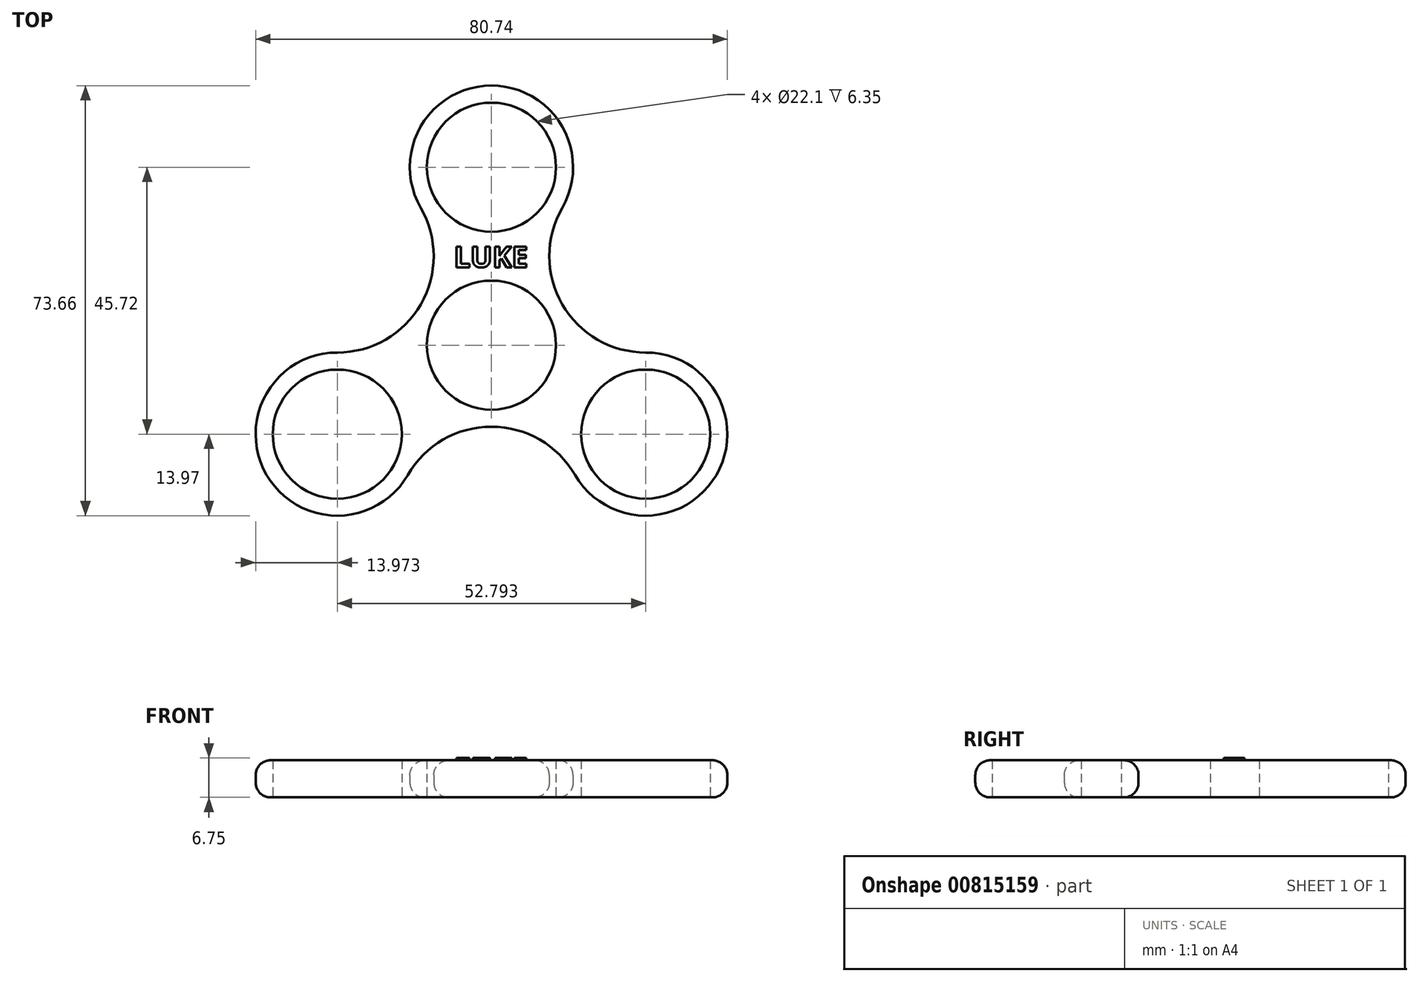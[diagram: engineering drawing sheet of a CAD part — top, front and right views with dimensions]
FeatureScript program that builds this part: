
annotation { "Feature Type Name" : "Feature", "Feature Type Description" : "" }
export const myFeature = defineFeature(function(context is Context, id is Id, definition is map)
    precondition{}
    {
        {
            var Q0;
            Q0=qCreatedBy(makeId("Top.planeOp"),FACE);
            var sketch = newSketch(context, id + "F0", { "sketchPlane" : qUnion([Q0])});
            skCircle(sketch, "E0", {"center": v(0, 0) * mm, "radius": 11.05 * mm});
            skCircle(sketch, "E1", {"center": v(0, 0) * mm, "radius": 13.97 * mm});
            skLineSegment(sketch, "E2", {"start": v(0, 11.05) * mm, "end": v(0, 19.43) * mm});
            skCircle(sketch, "E3", {"center": v(0, 30.48) * mm, "radius": 11.05 * mm});
            skCircle(sketch, "E4", {"center": v(0, 30.48) * mm, "radius": 13.97 * mm});
            skCircle(sketch, "E5.1.0", {"center": v(-26.4, -15.24) * mm, "radius": 11.05 * mm});
            skCircle(sketch, "E5.1.1", {"center": v(-26.4, -15.24) * mm, "radius": 13.97 * mm});
            skCircle(sketch, "E5.2.0", {"center": v(26.4, -15.24) * mm, "radius": 11.05 * mm});
            skCircle(sketch, "E5.2.1", {"center": v(26.4, -15.24) * mm, "radius": 13.97 * mm});
            skLineSegment(sketch, "E6", {"start": v(-9.57, 5.52) * mm, "end": v(-12.1, 6.99) * mm});
            skArc(sketch, "E7", {"start": v(-26.4, -1.27) * mm, "mid": v(-12.1, 6.99) * mm, "end": v(-12.1, 23.5) * mm});
            skArc(sketch, "E8.1.0", {"start": v(14.3, -22.23) * mm, "mid": v(0, -13.97) * mm, "end": v(-14.3, -22.22) * mm});
            skArc(sketch, "E8.2.0", {"start": v(12.1, 23.5) * mm, "mid": v(12.1, 6.98) * mm, "end": v(26.4, -1.27) * mm});
            skSolve(sketch);
        }
        {
            var Q0;
            Q0 = qSketchRegion(id + "F0", true);
            extrude(context, id + "F1", {"entities" : qUnion([Q0]), "depth" : 6.35 * mm, "offsetDistance" : 25.4 * mm});
        }
        {
            var Q0;
            Q0=makeQuery(id+"F1.opExtrude","CAP_EDGE",EDGE,{"disambiguationData":[OSD([sQuery(id+"F0.wireOp",EDGE,"E8.1.0")])],"isStart":false});
            var Q1;
            Q1=makeQuery(id+"F1.opExtrude","CAP_EDGE",EDGE,{"disambiguationData":[OSD([sQuery(id+"F0.wireOp",EDGE,"E7")])],"isStart":true});
            fillet(context, id + "F2", {"entities" : qUnion([Q0, Q1]), "radius" : 2.54 * mm, "tangentPropagation" : true, "allowEdgeOverflow" : false});
        }
        {
            var Q0;
            Q0=makeQuery(id+"F1.opExtrude","CAP_FACE",FACE,{"disambiguationData":[OSD([sQuery(id+"F0.wireOp",EDGE,"E0"),sQuery(id+"F0.wireOp",EDGE,"E3"),sQuery(id+"F0.wireOp",EDGE,"E4"),sQuery(id+"F0.wireOp",EDGE,"E5.1.0"),sQuery(id+"F0.wireOp",EDGE,"E5.1.1"),sQuery(id+"F0.wireOp",EDGE,"E5.2.0"),sQuery(id+"F0.wireOp",EDGE,"E5.2.1"),sQuery(id+"F0.wireOp",EDGE,"E7"),sQuery(id+"F0.wireOp",EDGE,"E8.1.0"),sQuery(id+"F0.wireOp",EDGE,"E8.2.0")])],"isStart":false});
            var sketch = newSketch(context, id + "F3", { "sketchPlane" : qUnion([Q0])});
            skText(sketch, "E9", { "text": "LUKE", "fontName": "OpenSans-Bold.ttf"});
            const initialGuessF3  = {"E9": [-0.00642, 0.01333, 1, 0, 0.00358]};
            skSetInitialGuess(sketch, initialGuessF3);
            skSolve(sketch);
        }
        {
            var Q0;
            Q0 = qSketchRegion(id + "F3", true);
            extrude(context, id + "F4", {"entities" : qUnion([Q0]), "operationType" : NewBodyOperationType.ADD, "depth" : 0.4 * mm, "offsetDistance" : 25.4 * mm});
        }
    });
